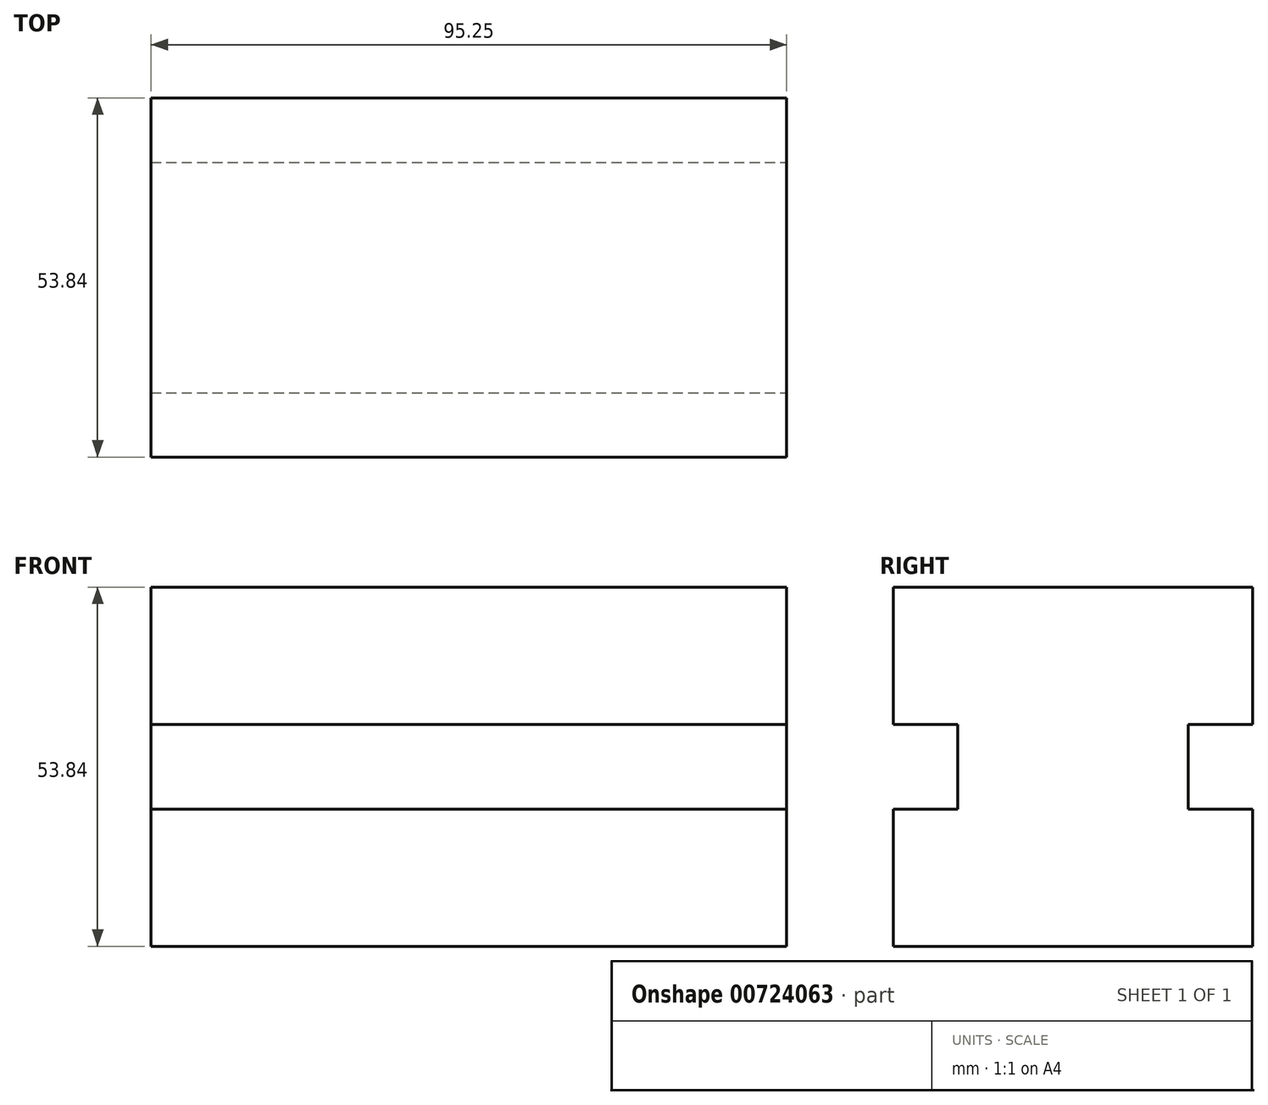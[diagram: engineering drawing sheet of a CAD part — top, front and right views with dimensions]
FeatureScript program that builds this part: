
annotation { "Feature Type Name" : "Feature", "Feature Type Description" : "" }
export const myFeature = defineFeature(function(context is Context, id is Id, definition is map)
    precondition{}
    {
        {
            var Q0;
            Q0=qCreatedBy(makeId("Right.planeOp"),FACE);
            var sketch = newSketch(context, id + "F0", { "sketchPlane" : qUnion([Q0])});
            skLineSegment(sketch, "E0.bottom", {"start": v(26.92, -26.92) * mm, "end": v(-26.92, -26.92) * mm});
            skLineSegment(sketch, "E0.top", {"start": v(26.92, 26.92) * mm, "end": v(-26.92, 26.92) * mm});
            skLineSegment(sketch, "E0.left", {"start": v(26.92, -26.92) * mm, "end": v(26.92, -6.35) * mm});
            skLineSegment(sketch, "E0.right", {"start": v(-26.92, -26.92) * mm, "end": v(-26.92, -6.35) * mm});
            skPoint(sketch, "E0.middle", {"position": v(0, 0) * mm});
            skLineSegment(sketch, "E1.bottom", {"start": v(-26.92, 6.35) * mm, "end": v(-17.27, 6.35) * mm});
            skLineSegment(sketch, "E1.top", {"start": v(-26.92, -6.35) * mm, "end": v(-17.27, -6.35) * mm});
            skLineSegment(sketch, "E1.right", {"start": v(-17.27, 6.35) * mm, "end": v(-17.27, -6.35) * mm});
            skLineSegment(sketch, "E2.trimOffspring", {"start": v(-26.92, 6.35) * mm, "end": v(-26.92, 26.92) * mm});
            skLineSegment(sketch, "E3", {"start": v(0, 66.4) * mm, "end": v(0, -63.15) * mm, "construction": true});
            skLineSegment(sketch, "E4.MirrorCS", {"start": v(26.92, 6.35) * mm, "end": v(17.27, 6.35) * mm});
            skLineSegment(sketch, "E5.MirrorCS", {"start": v(17.27, 6.35) * mm, "end": v(17.27, -6.35) * mm});
            skLineSegment(sketch, "E6.MirrorCS", {"start": v(26.92, -6.35) * mm, "end": v(17.27, -6.35) * mm});
            skLineSegment(sketch, "E7.trimOffspring", {"start": v(26.92, 6.35) * mm, "end": v(26.92, 26.92) * mm});
            skSolve(sketch);
        }
        {
            var Q0;
            Q0=makeQuery(id+"F0.imprint","IMPRINT",FACE,{"disambiguationData":[TD([[makeQuery(id+"F0.imprint","IMPRINT",EDGE,{"derivedFrom":sQuery(id+"F0.wireOp",EDGE,"E0.bottom")}),-1.0]])]});
            extrude(context, id + "F1", {"entities" : qUnion([Q0]), "oppositeDirection" : true, "depth" : 95.25 * mm, "offsetDistance" : 25.4 * mm});
        }
    });
